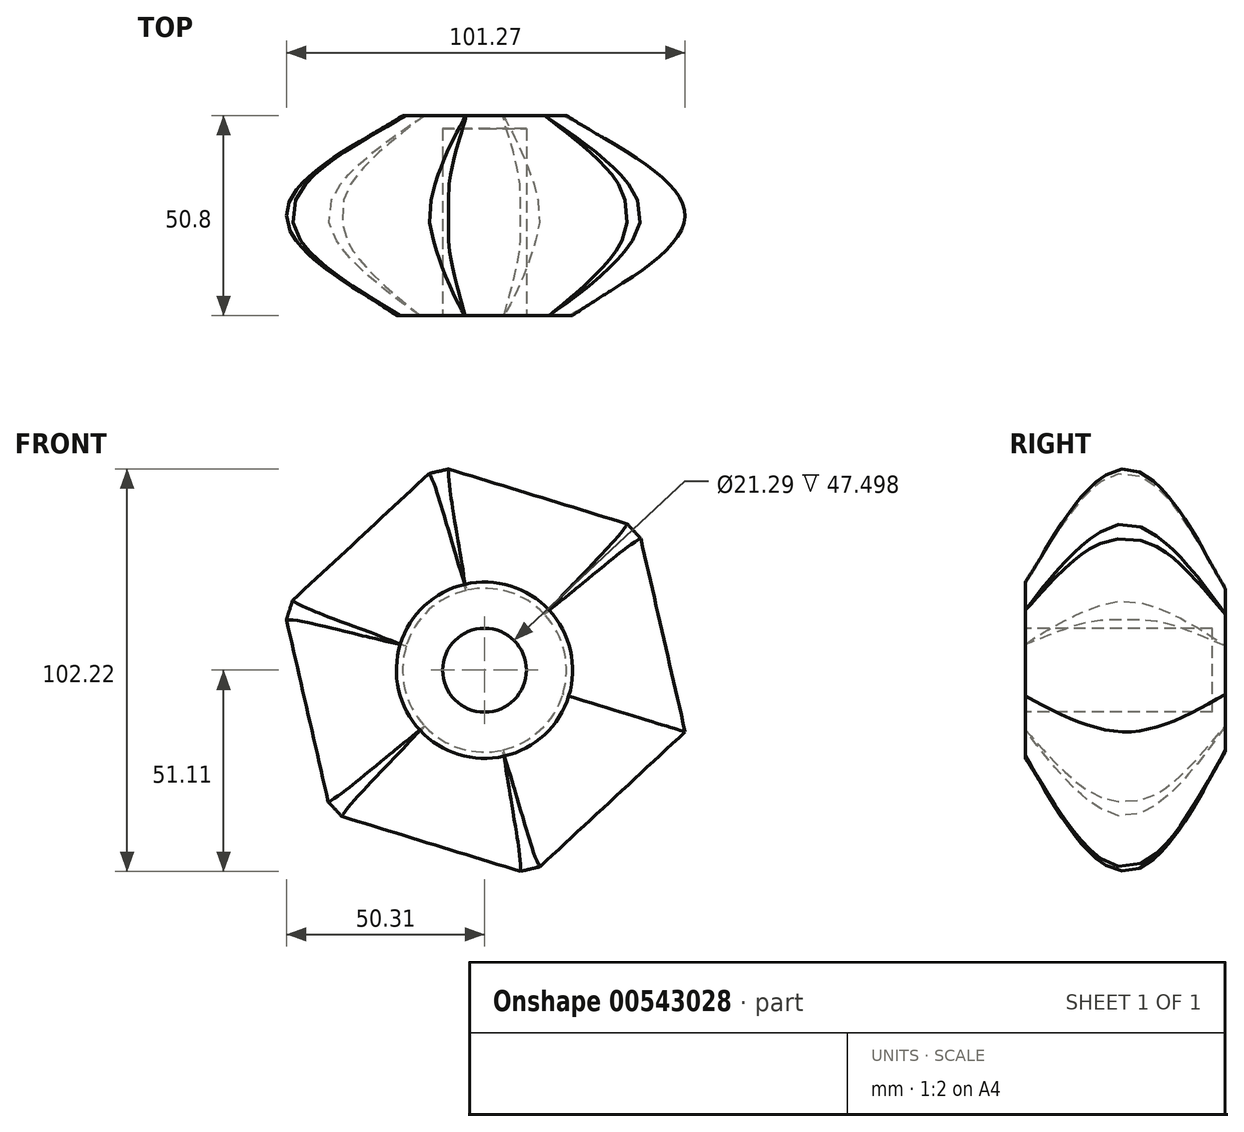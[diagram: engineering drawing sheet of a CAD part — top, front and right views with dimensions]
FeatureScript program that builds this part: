
annotation { "Feature Type Name" : "Feature", "Feature Type Description" : "" }
export const myFeature = defineFeature(function(context is Context, id is Id, definition is map)
    precondition{}
    {
        {
            var Q0;
            Q0=qCreatedBy(makeId("Front.planeOp"),FACE);
            var sketch = newSketch(context, id + "F0", { "sketchPlane" : qUnion([Q0])});
            skCircle(sketch, "E0", {"center": v(0, 0) * mm, "radius": 20.8 * mm});
            skSolve(sketch);
        }
        {
            var Q0;
            Q0=qCreatedBy(makeId("Front.planeOp"),FACE);
            cPlane(context, id + "F1", {"entities" : qUnion([Q0]), "cplaneType" : CPlaneType.OFFSET, "offset" : 25.4 * mm, "width" : 152.4 * mm, "height" : 152.4 * mm});
        }
        {
            var Q0;
            Q0=qCreatedBy(id+"F1.planeOp",FACE);
            var sketch = newSketch(context, id + "F2", { "sketchPlane" : qUnion([Q0])});
            skCircle(sketch, "E1.cCircle", {"center": v(0, 0) * mm, "radius": 46.17 * mm, "construction": true});
            skLineSegment(sketch, "E1.0", {"start": v(39.05, 36.3) * mm, "end": v(50.96, -15.67) * mm});
            skLineSegment(sketch, "E1.1", {"start": v(50.96, -15.67) * mm, "end": v(11.9, -51.97) * mm});
            skLineSegment(sketch, "E1.2", {"start": v(11.9, -51.97) * mm, "end": v(-39.05, -36.3) * mm});
            skLineSegment(sketch, "E1.3", {"start": v(-39.05, -36.3) * mm, "end": v(-50.96, 15.67) * mm});
            skLineSegment(sketch, "E1.4", {"start": v(-50.96, 15.67) * mm, "end": v(-11.9, 51.97) * mm});
            skLineSegment(sketch, "E1.5", {"start": v(-11.9, 51.97) * mm, "end": v(39.05, 36.3) * mm});
            skPoint(sketch, "E1.0.midPoint", {"position": v(45, 10.31) * mm});
            skSolve(sketch);
        }
        {
            var Q0;
            Q0=qCreatedBy(id+"F1.planeOp",FACE);
            cPlane(context, id + "F3", {"entities" : qUnion([Q0]), "cplaneType" : CPlaneType.OFFSET, "offset" : 25.4 * mm, "width" : 152.4 * mm, "height" : 152.4 * mm});
        }
        {
            var Q0;
            Q0=qCreatedBy(id+"F3.planeOp",FACE);
            var sketch = newSketch(context, id + "F4", { "sketchPlane" : qUnion([Q0])});
            skCircle(sketch, "E2", {"center": v(0, 0) * mm, "radius": 22.39 * mm});
            skSolve(sketch);
        }
        {
            var Q0;
            Q0=makeQuery(id+"F4.imprint","IMPRINT",FACE,{"disambiguationData":[TD([[makeQuery(id+"F4.imprint","IMPRINT",EDGE,{"derivedFrom":sQuery(id+"F4.wireOp",EDGE,"E2")}),1.0]])]});
            var Q1;
            Q1=makeQuery(id+"F2.imprint","IMPRINT",FACE,{"disambiguationData":[TD([[makeQuery(id+"F2.imprint","IMPRINT",EDGE,{"derivedFrom":sQuery(id+"F2.wireOp",EDGE,"E1.0")}),-1.0]])]});
            var Q2;
            Q2=makeQuery(id+"F0.imprint","IMPRINT",FACE,{"disambiguationData":[TD([[makeQuery(id+"F0.imprint","IMPRINT",EDGE,{"derivedFrom":sQuery(id+"F0.wireOp",EDGE,"E0")}),1.0]])]});
            loft(context, id + "F5", {"sheetProfilesArray" : [{ "sheetProfileEntities" : qUnion([Q0]) }, { "sheetProfileEntities" : qUnion([Q1]) }, { "sheetProfileEntities" : qUnion([Q2]) }]});
        }
        {
            var Q0;
            Q0=makeQuery(id+"F5.opLoft","CAP_FACE",FACE,{"disambiguationData":[OSD([makeQuery(id+"F4.imprint","IMPRINT",FACE,{"disambiguationData":[TD([[makeQuery(id+"F4.imprint","IMPRINT",EDGE,{"derivedFrom":sQuery(id+"F4.wireOp",EDGE,"E2")}),1.0]])]})])],"isStart":true});
            var sketch = newSketch(context, id + "F6", { "sketchPlane" : qUnion([Q0])});
            skCircle(sketch, "E3", {"center": v(0, 0) * mm, "radius": 10.65 * mm});
            skSolve(sketch);
        }
        {
            var Q0;
            Q0=makeQuery(id+"F6.imprint","IMPRINT",FACE,{"disambiguationData":[TD([[makeQuery(id+"F6.imprint","IMPRINT",EDGE,{"derivedFrom":sQuery(id+"F6.wireOp",EDGE,"E3")}),1.0]])]});
            extrude(context, id + "F7", {"entities" : qUnion([Q0]), "operationType" : NewBodyOperationType.REMOVE, "oppositeDirection" : true, "depth" : 47.5 * mm, "offsetDistance" : 25.4 * mm});
        }
        {
            var Q0;
            Q0=makeQuery(id+"F5.opLoft","SWEPT_EDGE",EDGE,{"disambiguationData":[OSD([sQuery(id+"F2.wireOp",EDGE,"E1.0"),sQuery(id+"F2.wireOp",EDGE,"E1.1"),sQuery(id+"F2.wireOp",EDGE,"E1.5"),sQuery(id+"F4.wireOp",EDGE,"E2")])]});
            var Q1;
            Q1=makeQuery(id+"F5.opLoft","SWEPT_EDGE",EDGE,{"disambiguationData":[OSD([sQuery(id+"F2.wireOp",EDGE,"E1.0"),sQuery(id+"F2.wireOp",EDGE,"E1.5")]),OD(1.0)]});
            var Q2;
            Q2=makeQuery(id+"F5.opLoft","SWEPT_EDGE",EDGE,{"disambiguationData":[OSD([sQuery(id+"F2.wireOp",EDGE,"E1.3"),sQuery(id+"F2.wireOp",EDGE,"E1.4"),sQuery(id+"F2.wireOp",EDGE,"E1.5"),sQuery(id+"F4.wireOp",EDGE,"E2")])]});
            var Q3;
            Q3=makeQuery(id+"F5.opLoft","SWEPT_EDGE",EDGE,{"disambiguationData":[OSD([sQuery(id+"F2.wireOp",EDGE,"E1.0"),sQuery(id+"F2.wireOp",EDGE,"E1.1"),sQuery(id+"F2.wireOp",EDGE,"E1.2"),sQuery(id+"F4.wireOp",EDGE,"E2")])]});
            var Q4;
            Q4=makeQuery(id+"F5.opLoft","SWEPT_EDGE",EDGE,{"disambiguationData":[OSD([sQuery(id+"F2.wireOp",EDGE,"E1.1"),sQuery(id+"F2.wireOp",EDGE,"E1.2"),sQuery(id+"F2.wireOp",EDGE,"E1.3"),sQuery(id+"F4.wireOp",EDGE,"E2")])]});
            var Q5;
            Q5=makeQuery(id+"F7.boolean.opBoolean","COPY",EDGE,{"derivedFrom":makeQuery(id+"F7.opExtrude","CAP_EDGE",EDGE,{"disambiguationData":[OSD([sQuery(id+"F6.wireOp",EDGE,"E3")])],"isStart":true})});
            var Q6;
            Q6=makeQuery(id+"F5.opLoft","SWEPT_EDGE",EDGE,{"disambiguationData":[OSD([sQuery(id+"F2.wireOp",EDGE,"E1.2"),sQuery(id+"F2.wireOp",EDGE,"E1.3"),sQuery(id+"F2.wireOp",EDGE,"E1.4"),sQuery(id+"F4.wireOp",EDGE,"E2")])]});
            chamfer(context, id + "F8", {"entities" : qUnion([Q0, Q1, Q2, Q3, Q4, Q5, Q6]), "width" : 5.08 * mm, "tangentPropagation" : true});
        }
    });
